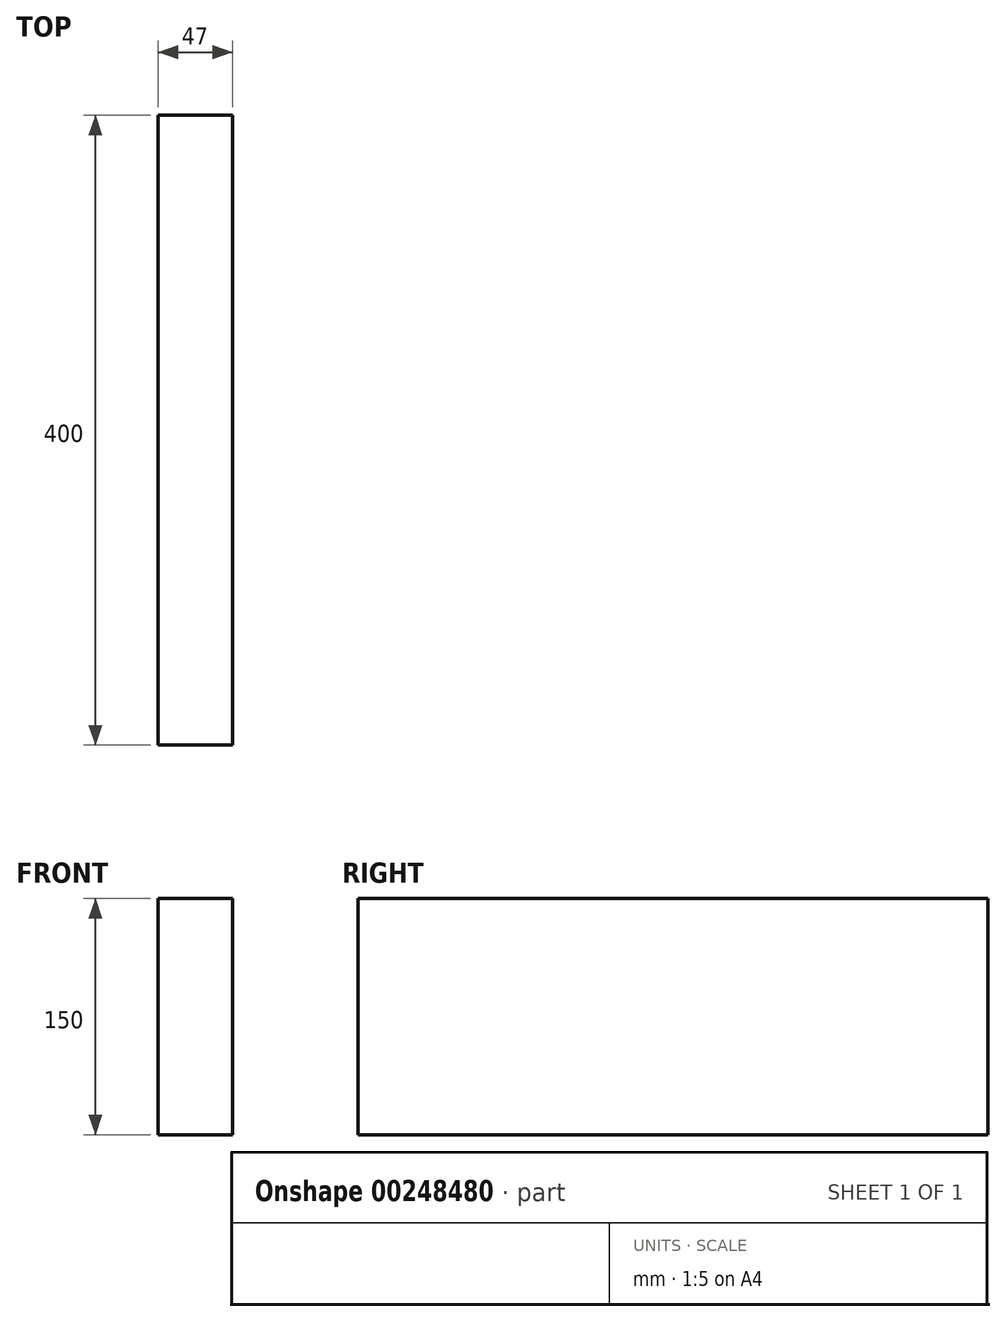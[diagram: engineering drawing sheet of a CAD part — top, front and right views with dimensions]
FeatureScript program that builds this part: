
annotation { "Feature Type Name" : "Feature", "Feature Type Description" : "" }
export const myFeature = defineFeature(function(context is Context, id is Id, definition is map)
    precondition{}
    {
        {
            var Q0;
            Q0=qCreatedBy(makeId("Front.planeOp"),FACE);
            var sketch = newSketch(context, id + "F0", { "sketchPlane" : qUnion([Q0])});
            skLineSegment(sketch, "E0.bottom", {"start": v(0, 0) * mm, "end": v(47, 0) * mm});
            skLineSegment(sketch, "E0.top", {"start": v(0, 150) * mm, "end": v(47, 150) * mm});
            skLineSegment(sketch, "E0.left", {"start": v(0, 0) * mm, "end": v(0, 150) * mm});
            skLineSegment(sketch, "E0.right", {"start": v(47, 0) * mm, "end": v(47, 150) * mm});
            skSolve(sketch);
        }
        {
            var Q0;
            Q0=makeQuery(id+"F0.imprint","IMPRINT",FACE,{"disambiguationData":[TD([[makeQuery(id+"F0.imprint","IMPRINT",EDGE,{"derivedFrom":sQuery(id+"F0.wireOp",EDGE,"E0.bottom")}),1.0]])]});
            extrude(context, id + "F1", {"entities" : qUnion([Q0]), "oppositeDirection" : true, "depth" : 400 * mm});
        }
    });
